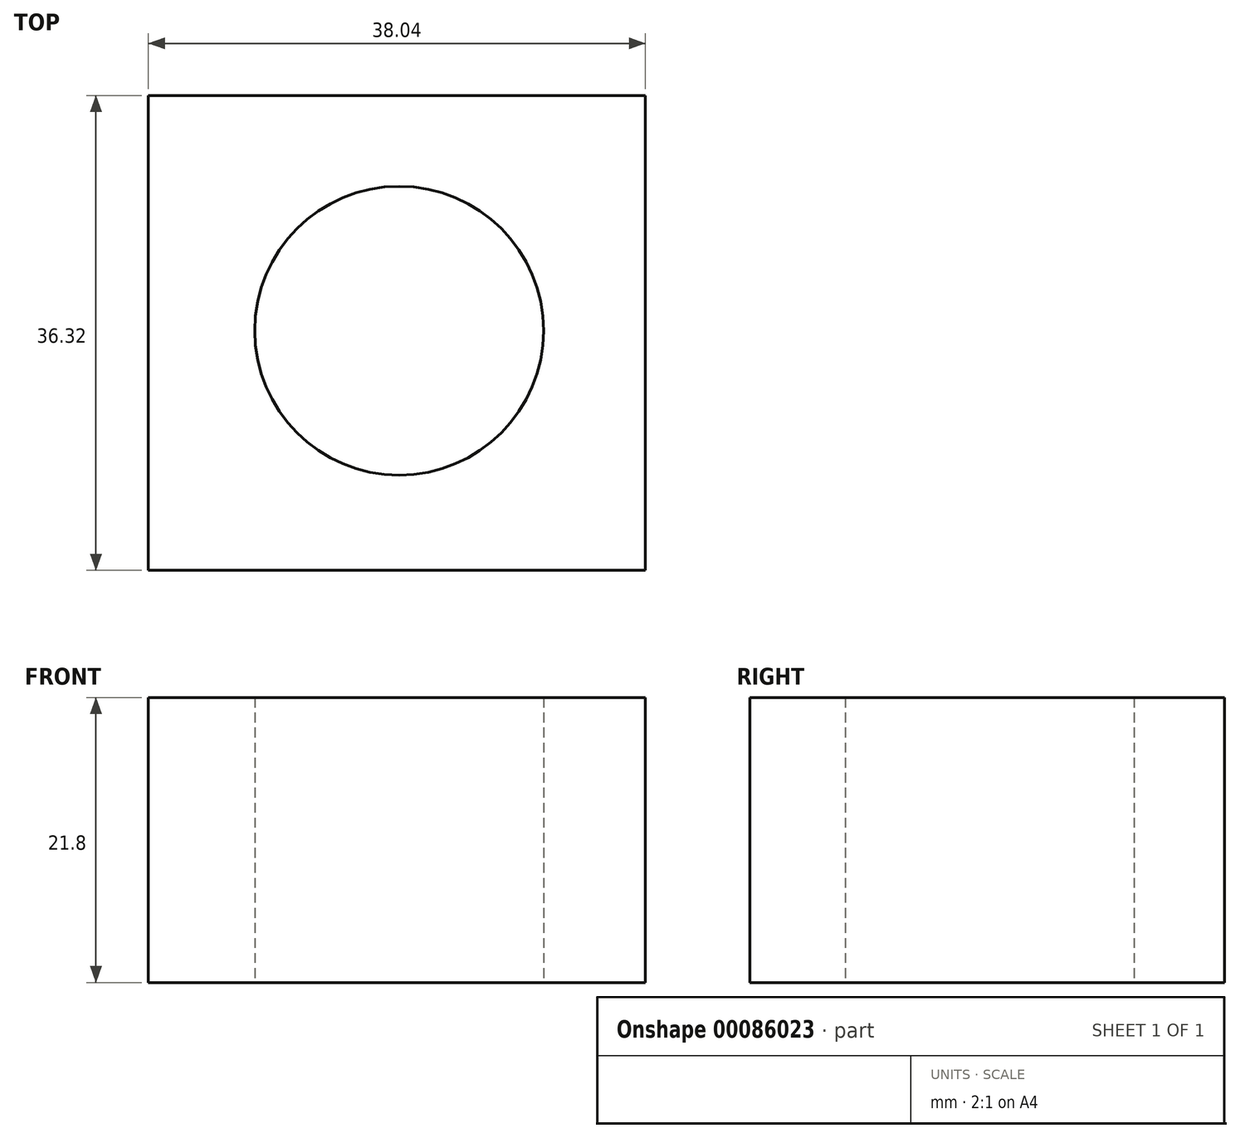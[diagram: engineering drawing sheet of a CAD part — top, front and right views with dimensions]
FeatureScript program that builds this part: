
annotation { "Feature Type Name" : "Feature", "Feature Type Description" : "" }
export const myFeature = defineFeature(function(context is Context, id is Id, definition is map)
    precondition{}
    {
        {
            var Q0;
            Q0=qCreatedBy(makeId("Top.planeOp"),FACE);
            var sketch = newSketch(context, id + "F0", { "sketchPlane" : qUnion([Q0])});
            skCircle(sketch, "E0", {"center": v(0, 0) * mm, "radius": 11.05 * mm});
            skLineSegment(sketch, "E1.bottom", {"start": v(-19.19, 17.99) * mm, "end": v(18.85, 17.99) * mm});
            skLineSegment(sketch, "E1.top", {"start": v(-19.19, -18.33) * mm, "end": v(18.85, -18.33) * mm});
            skLineSegment(sketch, "E1.left", {"start": v(-19.19, 17.99) * mm, "end": v(-19.19, -18.33) * mm});
            skLineSegment(sketch, "E1.right", {"start": v(18.85, 17.99) * mm, "end": v(18.85, -18.33) * mm});
            skSolve(sketch);
        }
        {
            var Q0;
            Q0=makeQuery(id+"F0.imprint","IMPRINT",FACE,{"disambiguationData":[TD([[makeQuery(id+"F0.imprint","IMPRINT",EDGE,{"derivedFrom":sQuery(id+"F0.wireOp",EDGE,"E0")}),-1.0]])]});
            extrude(context, id + "F1", {"entities" : qUnion([Q0]), "depth" : 21.8 * mm});
        }
    });
